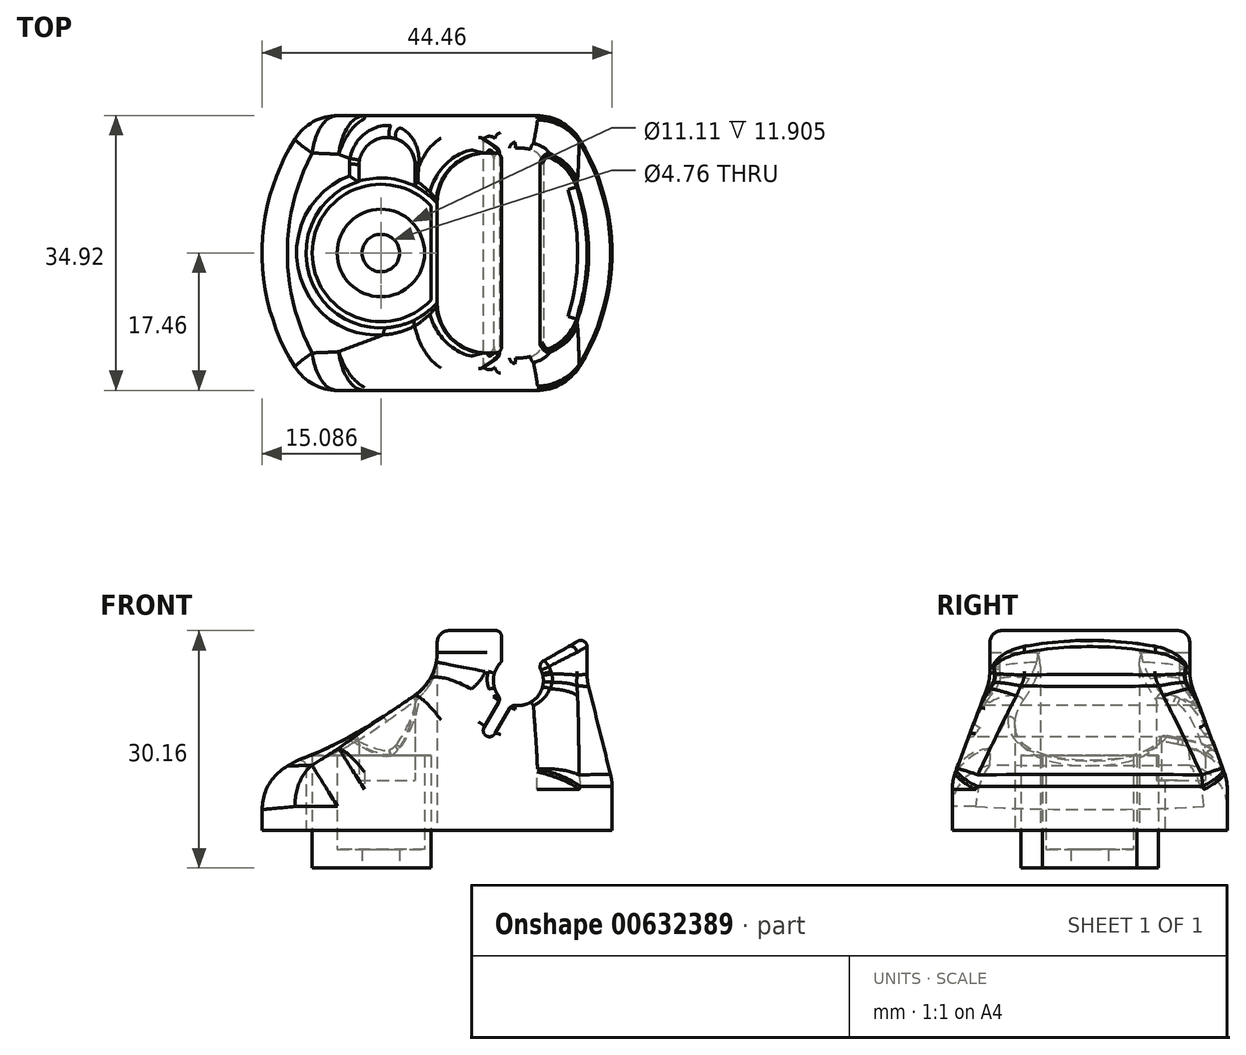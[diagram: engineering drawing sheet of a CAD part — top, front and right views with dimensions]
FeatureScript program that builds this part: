
annotation { "Feature Type Name" : "Feature", "Feature Type Description" : "" }
export const myFeature = defineFeature(function(context is Context, id is Id, definition is map)
    precondition{}
    {
        {
            var Q0;
            Q0=qCreatedBy(makeId("Top.planeOp"),FACE);
            var sketch = newSketch(context, id + "F0", { "sketchPlane" : qUnion([Q0])});
            skLineSegment(sketch, "E0.bottom", {"start": v(22.23, 17.46) * mm, "end": v(15.88, 17.46) * mm, "construction": true});
            skLineSegment(sketch, "E0.top", {"start": v(22.23, -17.46) * mm, "end": v(15.88, -17.46) * mm, "construction": true});
            skLineSegment(sketch, "E0.left", {"start": v(22.23, 17.46) * mm, "end": v(22.23, -17.46) * mm, "construction": true});
            skLineSegment(sketch, "E0.right", {"start": v(-22.22, 17.46) * mm, "end": v(-22.22, -17.46) * mm, "construction": true});
            skPoint(sketch, "E0.middle", {"position": v(0, 0) * mm});
            skArc(sketch, "E1", {"start": v(15.88, -17.46) * mm, "mid": v(22.23, 0) * mm, "end": v(15.88, 17.46) * mm});
            skLineSegment(sketch, "E2", {"start": v(15.88, 17.46) * mm, "end": v(-15.87, 17.46) * mm});
            skLineSegment(sketch, "E3", {"start": v(15.88, -17.46) * mm, "end": v(-15.87, -17.46) * mm});
            skPoint(sketch, "E4.visualSharp", {"position": v(15.88, 17.46) * mm});
            skPoint(sketch, "E5.visualSharp", {"position": v(15.88, -17.46) * mm});
            skArc(sketch, "E6", {"start": v(-15.88, 17.46) * mm, "mid": v(-22.22, 0) * mm, "end": v(-15.87, -17.46) * mm});
            skLineSegment(sketch, "E7", {"start": v(-15.87, 17.46) * mm, "end": v(-22.22, 17.46) * mm, "construction": true});
            skLineSegment(sketch, "E8", {"start": v(-15.87, -17.46) * mm, "end": v(-22.22, -17.46) * mm, "construction": true});
            skPoint(sketch, "E9.visualSharp", {"position": v(-15.87, 17.46) * mm});
            skPoint(sketch, "E10.visualSharp", {"position": v(-15.87, -17.46) * mm});
            skSolve(sketch);
        }
        {
            var Q0;
            Q0=makeQuery(id+"F0.imprint","IMPRINT",FACE,{"disambiguationData":[TD([[makeQuery(id+"F0.imprint","IMPRINT",EDGE,{"derivedFrom":sQuery(id+"F0.wireOp",EDGE,"E1")}),1.0]])]});
            extrude(context, id + "F1", {"entities" : qUnion([Q0]), "depth" : 6.35 * mm, "offsetDistance" : 25.4 * mm});
        }
        {
            var Q0;
            Q0=qCreatedBy(makeId("Top.planeOp"),FACE);
            cPlane(context, id + "F2", {"entities" : qUnion([Q0]), "cplaneType" : CPlaneType.OFFSET, "offset" : 19.05 * mm, "width" : 152.4 * mm, "height" : 152.4 * mm});
        }
        {
            var Q0;
            Q0=qCreatedBy(id+"F2.planeOp",FACE);
            var sketch = newSketch(context, id + "F3", { "sketchPlane" : qUnion([Q0])});
            skLineSegment(sketch, "E11.bottom", {"start": v(0, 12.7) * mm, "end": v(15.9, 12.7) * mm});
            skLineSegment(sketch, "E11.top", {"start": v(0, -12.7) * mm, "end": v(15.9, -12.7) * mm});
            skLineSegment(sketch, "E11.left", {"start": v(0, 12.7) * mm, "end": v(0, -12.7) * mm});
            skLineSegment(sketch, "E11.right", {"start": v(19.05, 12.7) * mm, "end": v(19.05, -12.7) * mm, "construction": true});
            skArc(sketch, "E12", {"start": v(15.9, -12.7) * mm, "mid": v(19.05, 0) * mm, "end": v(15.9, 12.7) * mm});
            skPoint(sketch, "E13.visualSharp", {"position": v(0, 12.7) * mm});
            skPoint(sketch, "E14.visualSharp", {"position": v(0, -12.7) * mm});
            skSolve(sketch);
        }
        {
            var Q1;
            Q1=makeQuery(id+"F1.opExtrude","CAP_FACE",FACE,{"disambiguationData":[OSD([sQuery(id+"F0.wireOp",EDGE,"E1"),sQuery(id+"F0.wireOp",EDGE,"E2"),sQuery(id+"F0.wireOp",EDGE,"E3"),sQuery(id+"F0.wireOp",EDGE,"E4.filletArc"),sQuery(id+"F0.wireOp",EDGE,"E5.filletArc"),sQuery(id+"F0.wireOp",EDGE,"E6"),sQuery(id+"F0.wireOp",EDGE,"E9.filletArc"),sQuery(id+"F0.wireOp",EDGE,"E10.filletArc")])],"isStart":false});
            var Q2;
            Q2=makeQuery(id+"F3.imprint","IMPRINT",FACE,{"disambiguationData":[TD([[makeQuery(id+"F3.imprint","IMPRINT",EDGE,{"derivedFrom":sQuery(id+"F3.wireOp",EDGE,"E11.bottom")}),-1.0]])]});
            loft(context, id + "F4", {"operationType" : NewBodyOperationType.ADD, "sheetProfilesArray" : [{ "sheetProfileEntities" : qUnion([Q1]) }, { "sheetProfileEntities" : qUnion([Q2]) }]});
        }
        {
            var Q0;
            Q0=makeQuery(id+"F4.opLoft","CAP_FACE",FACE,{"disambiguationData":[OSD([makeQuery(id+"F3.imprint","IMPRINT",FACE,{"disambiguationData":[TD([[makeQuery(id+"F3.imprint","IMPRINT",EDGE,{"derivedFrom":sQuery(id+"F3.wireOp",EDGE,"E11.bottom")}),-1.0]])]})])],"isStart":true});
            extrude(context, id + "F5", {"entities" : qUnion([Q0]), "operationType" : NewBodyOperationType.ADD, "flatOperationType" : FlatOperationType.REMOVE, "depth" : 6.35 * mm, "offsetDistance" : 25.4 * mm, "domain" : OperationDomain.MODEL});
        }
        {
            var Q0;
            Q0=makeQuery(id+"F4.opLoft","SWEPT_EDGE",EDGE,{"disambiguationData":[OSD([sQuery(id+"F0.wireOp",EDGE,"E2"),sQuery(id+"F0.wireOp",EDGE,"E6"),sQuery(id+"F3.wireOp",EDGE,"E11.bottom"),sQuery(id+"F3.wireOp",EDGE,"E11.left")])]});
            var Q1;
            Q1=makeQuery(id+"F1.opExtrude","SWEPT_EDGE",EDGE,{"disambiguationData":[OSD([sQuery(id+"F0.wireOp",EDGE,"E2"),sQuery(id+"F0.wireOp",EDGE,"E6")])]});
            var Q2;
            Q2=makeQuery(id+"F5.opExtrude","SWEPT_EDGE",EDGE,{"disambiguationData":[OSD([sQuery(id+"F3.wireOp",EDGE,"E11.bottom"),sQuery(id+"F3.wireOp",EDGE,"E11.left")])]});
            var Q3;
            Q3=makeQuery(id+"F4.opLoft","SWEPT_EDGE",EDGE,{"disambiguationData":[OSD([sQuery(id+"F0.wireOp",EDGE,"E3"),sQuery(id+"F0.wireOp",EDGE,"E6"),sQuery(id+"F3.wireOp",EDGE,"E11.top"),sQuery(id+"F3.wireOp",EDGE,"E11.left")])]});
            var Q4;
            Q4=makeQuery(id+"F5.opExtrude","SWEPT_EDGE",EDGE,{"disambiguationData":[OSD([sQuery(id+"F3.wireOp",EDGE,"E11.top"),sQuery(id+"F3.wireOp",EDGE,"E11.left")])]});
            var Q5;
            Q5=makeQuery(id+"F1.opExtrude","SWEPT_EDGE",EDGE,{"disambiguationData":[OSD([sQuery(id+"F0.wireOp",EDGE,"E3"),sQuery(id+"F0.wireOp",EDGE,"E6")])]});
            var Q6;
            Q6=makeQuery(id+"F1.opExtrude","SWEPT_EDGE",EDGE,{"disambiguationData":[OSD([sQuery(id+"F0.wireOp",EDGE,"E1"),sQuery(id+"F0.wireOp",EDGE,"E3")])]});
            var Q7;
            Q7=makeQuery(id+"F4.opLoft","SWEPT_EDGE",EDGE,{"disambiguationData":[OSD([sQuery(id+"F0.wireOp",EDGE,"E1"),sQuery(id+"F0.wireOp",EDGE,"E3"),sQuery(id+"F3.wireOp",EDGE,"E11.top"),sQuery(id+"F3.wireOp",EDGE,"E12")])]});
            var Q8;
            Q8=makeQuery(id+"F5.opExtrude","SWEPT_EDGE",EDGE,{"disambiguationData":[OSD([sQuery(id+"F3.wireOp",EDGE,"E11.top"),sQuery(id+"F3.wireOp",EDGE,"E12")])]});
            var Q9;
            Q9=makeQuery(id+"F1.opExtrude","SWEPT_EDGE",EDGE,{"disambiguationData":[OSD([sQuery(id+"F0.wireOp",EDGE,"E1"),sQuery(id+"F0.wireOp",EDGE,"E2")])]});
            var Q10;
            Q10=makeQuery(id+"F4.opLoft","SWEPT_EDGE",EDGE,{"disambiguationData":[OSD([sQuery(id+"F0.wireOp",EDGE,"E1"),sQuery(id+"F0.wireOp",EDGE,"E2"),sQuery(id+"F3.wireOp",EDGE,"E11.bottom"),sQuery(id+"F3.wireOp",EDGE,"E12")])]});
            var Q11;
            Q11=makeQuery(id+"F5.opExtrude","SWEPT_EDGE",EDGE,{"disambiguationData":[OSD([sQuery(id+"F3.wireOp",EDGE,"E11.bottom"),sQuery(id+"F3.wireOp",EDGE,"E12")])]});
            var Q12;
            Q12=makeQuery(id+"F4.opLoft","SWEPT_FACE",FACE,{"disambiguationData":[OSD([sQuery(id+"F0.wireOp",EDGE,"E1"),sQuery(id+"F0.wireOp",EDGE,"E2"),sQuery(id+"F0.wireOp",EDGE,"E3"),sQuery(id+"F3.wireOp",EDGE,"E11.bottom"),sQuery(id+"F3.wireOp",EDGE,"E11.top"),sQuery(id+"F3.wireOp",EDGE,"E12")])]});
            var Q13;
            Q13=makeQuery(id+"F4.opLoft","SWEPT_FACE",FACE,{"disambiguationData":[OSD([sQuery(id+"F0.wireOp",EDGE,"E1"),sQuery(id+"F0.wireOp",EDGE,"E2"),sQuery(id+"F0.wireOp",EDGE,"E6"),sQuery(id+"F3.wireOp",EDGE,"E11.bottom"),sQuery(id+"F3.wireOp",EDGE,"E11.left"),sQuery(id+"F3.wireOp",EDGE,"E12")])]});
            var Q14;
            Q14=makeQuery(id+"F4.opLoft","SWEPT_FACE",FACE,{"disambiguationData":[OSD([sQuery(id+"F0.wireOp",EDGE,"E2"),sQuery(id+"F0.wireOp",EDGE,"E3"),sQuery(id+"F0.wireOp",EDGE,"E6"),sQuery(id+"F3.wireOp",EDGE,"E11.bottom"),sQuery(id+"F3.wireOp",EDGE,"E11.top"),sQuery(id+"F3.wireOp",EDGE,"E11.left")])]});
            var Q15;
            Q15=makeQuery(id+"F4.opLoft","SWEPT_FACE",FACE,{"disambiguationData":[OSD([sQuery(id+"F0.wireOp",EDGE,"E1"),sQuery(id+"F0.wireOp",EDGE,"E3"),sQuery(id+"F0.wireOp",EDGE,"E6"),sQuery(id+"F3.wireOp",EDGE,"E11.top"),sQuery(id+"F3.wireOp",EDGE,"E11.left"),sQuery(id+"F3.wireOp",EDGE,"E12")])]});
            fillet(context, id + "F6", {"entities" : qUnion([Q0, Q1, Q2, Q3, Q4, Q5, Q6, Q7, Q8, Q9, Q10, Q11, Q12, Q13, Q14, Q15]), "radius" : 6.35 * mm, "tangentPropagation" : true, "allowEdgeOverflow" : false});
        }
        {
            var Q0;
            Q0=makeQuery(id+"F5.opExtrude","CAP_EDGE",EDGE,{"disambiguationData":[OSD([sQuery(id+"F3.wireOp",EDGE,"E11.bottom"),sQuery(id+"F3.wireOp",EDGE,"E11.top"),sQuery(id+"F3.wireOp",EDGE,"E11.left")])],"isStart":false});
            fillet(context, id + "F7", {"entities" : qUnion([Q0]), "radius" : 1.59 * mm, "tangentPropagation" : true, "allowEdgeOverflow" : false});
        }
        {
            var Q0;
            Q0=qCreatedBy(makeId("Front.planeOp"),FACE);
            var sketch = newSketch(context, id + "F8", { "sketchPlane" : qUnion([Q0])});
            skArc(sketch, "E15", {"start": v(8.21, 21.42) * mm, "mid": v(7.15, 19.13) * mm, "end": v(8.1, 16.78) * mm});
            skLineSegment(sketch, "E16", {"start": v(22.23, 5.57) * mm, "end": v(22.23, 0) * mm, "construction": true});
            skLineSegment(sketch, "E17", {"start": v(8.21, 21.42) * mm, "end": v(8.21, 25.4) * mm});
            skLineSegment(sketch, "E18", {"start": v(8.1, 16.78) * mm, "end": v(5.97, 13.1) * mm});
            skArc(sketch, "E19", {"start": v(5.97, 13.1) * mm, "mid": v(6.26, 12.01) * mm, "end": v(7.34, 12.3) * mm});
            skLineSegment(sketch, "E20", {"start": v(7.34, 12.3) * mm, "end": v(9.47, 16) * mm});
            skLineSegment(sketch, "E21", {"start": v(6.65, 12.7) * mm, "end": v(10.32, 19.05) * mm, "construction": true});
            skArc(sketch, "E22.trimOffspring", {"start": v(9.47, 16) * mm, "mid": v(13, 17.33) * mm, "end": v(12.75, 21.1) * mm});
            skArc(sketch, "E23", {"start": v(19.05, 23.81) * mm, "mid": v(18.59, 24.94) * mm, "end": v(17.46, 25.4) * mm, "construction": true});
            skFitSpline(sketch, "E24.0", {"points": [v(16.24, 25.4) * mm, v(16.65, 25.4) * mm, v(17.06, 25.4) * mm, v(17.46, 25.4) * mm]});
            skLineSegment(sketch, "E25.0", {"start": v(11.7, 25.4) * mm, "end": v(16.24, 25.4) * mm});
            skLineSegment(sketch, "E26.0", {"start": v(8.21, 25.4) * mm, "end": v(11.7, 25.4) * mm});
            skPoint(sketch, "E27.orphan", {"position": v(6.35, 25.4) * mm});
            skLineSegment(sketch, "E28", {"start": v(12.75, 21.1) * mm, "end": v(20.21, 25.4) * mm});
            skLineSegment(sketch, "E29", {"start": v(20.21, 25.4) * mm, "end": v(17.46, 25.4) * mm});
            skSolve(sketch);
        }
        {
            var Q0;
            Q0=makeQuery(id+"F8.imprint","IMPRINT",FACE,{"disambiguationData":[TD([[makeQuery(id+"F8.imprint","IMPRINT",EDGE,{"derivedFrom":sQuery(id+"F8.wireOp",EDGE,"E15")}),1.0]])]});
            extrude(context, id + "F9", {"entities" : qUnion([Q0]), "operationType" : NewBodyOperationType.REMOVE, "endBound" : BoundingType.SYMMETRIC, "oppositeDirection" : true, "depth" : 50.8 * mm, "offsetDistance" : 25.4 * mm});
        }
        {
            var Q0;
            Q0=makeQuery(id+"F9.boolean.opBoolean","INTERSECT",EDGE,{"derivedFrom":[makeQuery(id+"F7.opFillet","BLEND_FACE",FACE,{"disambiguationData":[OSD([sQuery(id+"F3.wireOp",EDGE,"E11.bottom"),sQuery(id+"F3.wireOp",EDGE,"E11.top"),sQuery(id+"F3.wireOp",EDGE,"E12")])]}),makeQuery(id+"F9.opExtrude","SWEPT_FACE",FACE,{"disambiguationData":[OSD([sQuery(id+"F8.wireOp",EDGE,"E28")])]})]});
            var Q1;
            Q1=makeQuery(id+"F9.boolean.opBoolean","COPY",EDGE,{"derivedFrom":makeQuery(id+"F9.opExtrude","SWEPT_EDGE",EDGE,{"disambiguationData":[OSD([sQuery(id+"F8.wireOp",EDGE,"E22.trimOffspring"),sQuery(id+"F8.wireOp",EDGE,"E28")])]})});
            var Q2;
            Q2=makeQuery(id+"F9.boolean.opBoolean","INTERSECT",EDGE,{"derivedFrom":[makeQuery(id+"F6.opFillet","BLEND_FACE",FACE,{"disambiguationData":[OSD([sQuery(id+"F0.wireOp",EDGE,"E1"),sQuery(id+"F0.wireOp",EDGE,"E3")]),OD(1.0)]}),makeQuery(id+"F9.opExtrude","SWEPT_FACE",FACE,{"disambiguationData":[OSD([sQuery(id+"F8.wireOp",EDGE,"E22.trimOffspring")])]})]});
            var Q3;
            Q3=makeQuery(id+"F9.boolean.opBoolean","INTERSECT",EDGE,{"derivedFrom":[makeQuery(id+"F6.opFillet","BLEND_FACE",FACE,{"disambiguationData":[OSD([sQuery(id+"F0.wireOp",EDGE,"E1"),sQuery(id+"F0.wireOp",EDGE,"E2"),sQuery(id+"F3.wireOp",EDGE,"E11.bottom"),sQuery(id+"F3.wireOp",EDGE,"E12")])]}),makeQuery(id+"F9.opExtrude","SWEPT_FACE",FACE,{"disambiguationData":[OSD([sQuery(id+"F8.wireOp",EDGE,"E22.trimOffspring")])]})]});
            var Q4;
            Q4=makeQuery(id+"F9.boolean.opBoolean","COPY",FACE,{"derivedFrom":makeQuery(id+"F9.opExtrude","SWEPT_FACE",FACE,{"disambiguationData":[OSD([sQuery(id+"F8.wireOp",EDGE,"E20")])]})});
            var Q5;
            Q5=makeQuery(id+"F9.boolean.opBoolean","COPY",FACE,{"derivedFrom":makeQuery(id+"F9.opExtrude","SWEPT_FACE",FACE,{"disambiguationData":[OSD([sQuery(id+"F8.wireOp",EDGE,"E15")])]})});
            var Q6;
            Q6=makeQuery(id+"F9.boolean.opBoolean","COPY",EDGE,{"derivedFrom":makeQuery(id+"F9.opExtrude","SWEPT_EDGE",EDGE,{"disambiguationData":[OSD([sQuery(id+"F8.wireOp",EDGE,"E15"),sQuery(id+"F8.wireOp",EDGE,"E17")])]})});
            var Q7;
            Q7=makeQuery(id+"F9.boolean.opBoolean","COPY",FACE,{"derivedFrom":makeQuery(id+"F9.opExtrude","SWEPT_FACE",FACE,{"disambiguationData":[OSD([sQuery(id+"F8.wireOp",EDGE,"E17")])]})});
            fillet(context, id + "F10", {"entities" : qUnion([Q0, Q1, Q2, Q3, Q4, Q5, Q6, Q7]), "radius" : 0.8 * mm, "tangentPropagation" : true, "allowEdgeOverflow" : false});
        }
        {
            var Q0;
            Q0=makeQuery(id+"F1.opExtrude","CAP_FACE",FACE,{"disambiguationData":[OSD([sQuery(id+"F0.wireOp",EDGE,"E1"),sQuery(id+"F0.wireOp",EDGE,"E2"),sQuery(id+"F0.wireOp",EDGE,"E3"),sQuery(id+"F0.wireOp",EDGE,"E6")])],"isStart":true});
            var sketch = newSketch(context, id + "F11", { "sketchPlane" : qUnion([Q0])});
            skPoint(sketch, "E30.middle", {"position": v(-7.14, 0) * mm});
            skCircle(sketch, "E31", {"center": v(-7.14, 0) * mm, "radius": 5.56 * mm, "construction": true});
            skArc(sketch, "E32", {"start": v(0, 6.3) * mm, "mid": v(-16.67, 0) * mm, "end": v(0, -6.3) * mm});
            skLineSegment(sketch, "E33", {"start": v(0, 6.3) * mm, "end": v(0, -6.3) * mm});
            skSolve(sketch);
        }
        {
            var Q0;
            Q0=makeQuery(id+"F11.imprint","IMPRINT",FACE,{"disambiguationData":[TD([[makeQuery(id+"F11.imprint","IMPRINT",EDGE,{"derivedFrom":sQuery(id+"F11.wireOp",EDGE,"E32")}),1.0]])]});
            extrude(context, id + "F12", {"entities" : qUnion([Q0]), "operationType" : NewBodyOperationType.REMOVE, "oppositeDirection" : true, "depth" : 25.4 * mm, "offsetDistance" : 25.4 * mm});
        }
        {
            var Q0;
            Q0=makeQuery(id+"F1.opExtrude","CAP_FACE",FACE,{"disambiguationData":[OSD([sQuery(id+"F0.wireOp",EDGE,"E1"),sQuery(id+"F0.wireOp",EDGE,"E2"),sQuery(id+"F0.wireOp",EDGE,"E3"),sQuery(id+"F0.wireOp",EDGE,"E6")])],"isStart":true});
            cPlane(context, id + "F13", {"entities" : qUnion([Q0]), "cplaneType" : CPlaneType.OFFSET, "offset" : 6.35 * mm, "oppositeDirection" : true, "width" : 152.4 * mm, "height" : 152.4 * mm});
        }
        {
            var Q0;
            Q0=qCreatedBy(id+"F13.planeOp",FACE);
            var sketch = newSketch(context, id + "F14", { "sketchPlane" : qUnion([Q0])});
            skLineSegment(sketch, "E34", {"start": v(-6.35, 0) * mm, "end": v(-6.35, -11.11) * mm, "construction": true});
            skArc(sketch, "E35", {"start": v(-9.92, -11.11) * mm, "mid": v(-6.35, -14.68) * mm, "end": v(-2.78, -11.11) * mm});
            skLineSegment(sketch, "E36", {"start": v(-9.92, -11.11) * mm, "end": v(-9.92, 0) * mm});
            skLineSegment(sketch, "E37", {"start": v(-9.92, 0) * mm, "end": v(-2.78, 0) * mm});
            skLineSegment(sketch, "E38", {"start": v(-2.78, 0) * mm, "end": v(-2.78, -11.11) * mm});
            skSolve(sketch);
        }
        {
            var Q0;
            Q0=makeQuery(id+"F14.imprint","IMPRINT",FACE,{"disambiguationData":[TD([[makeQuery(id+"F14.imprint","IMPRINT",EDGE,{"derivedFrom":sQuery(id+"F14.wireOp",EDGE,"E35")}),1.0]])]});
            extrude(context, id + "F15", {"entities" : qUnion([Q0]), "operationType" : NewBodyOperationType.REMOVE, "oppositeDirection" : true, "depth" : 25.4 * mm, "offsetDistance" : 25.4 * mm});
        }
        {
            var Q0;
            Q0=makeQuery(id+"F12.boolean.opBoolean","INTERSECT",EDGE,{"derivedFrom":[makeQuery(id+"F4.opLoft","SWEPT_FACE",FACE,{"disambiguationData":[OSD([sQuery(id+"F0.wireOp",EDGE,"E2"),sQuery(id+"F0.wireOp",EDGE,"E3"),sQuery(id+"F0.wireOp",EDGE,"E6"),sQuery(id+"F3.wireOp",EDGE,"E11.bottom"),sQuery(id+"F3.wireOp",EDGE,"E11.top"),sQuery(id+"F3.wireOp",EDGE,"E11.left")])]}),makeQuery(id+"F12.opExtrude","SWEPT_FACE",FACE,{"disambiguationData":[OSD([sQuery(id+"F11.wireOp",EDGE,"E32")])]})]});
            var Q1;
            Q1=makeQuery(id+"F15.boolean.opBoolean","INTERSECT",EDGE,{"derivedFrom":[makeQuery(id+"F4.opLoft","SWEPT_FACE",FACE,{"disambiguationData":[OSD([sQuery(id+"F0.wireOp",EDGE,"E2"),sQuery(id+"F0.wireOp",EDGE,"E3"),sQuery(id+"F0.wireOp",EDGE,"E6"),sQuery(id+"F3.wireOp",EDGE,"E11.bottom"),sQuery(id+"F3.wireOp",EDGE,"E11.top"),sQuery(id+"F3.wireOp",EDGE,"E11.left")])]}),makeQuery(id+"F15.opExtrude","SWEPT_FACE",FACE,{"disambiguationData":[OSD([sQuery(id+"F14.wireOp",EDGE,"E36")])]})]});
            var Q2;
            Q2=makeQuery(id+"F12.boolean.opBoolean","INTERSECT",EDGE,{"disambiguationData":[OD(2.0)],"derivedFrom":[makeQuery(id+"F6.opFillet","BLEND_FACE",FACE,{"disambiguationData":[OSD([sQuery(id+"F3.wireOp",EDGE,"E11.bottom"),sQuery(id+"F3.wireOp",EDGE,"E11.top"),sQuery(id+"F3.wireOp",EDGE,"E11.left")])]}),makeQuery(id+"F12.opExtrude","SWEPT_FACE",FACE,{"disambiguationData":[OSD([sQuery(id+"F11.wireOp",EDGE,"E32")])]})]});
            var Q3;
            Q3=makeQuery(id+"Fa9YRneLped70sL_1.1.F15.boolean.opBoolean","INTERSECT",EDGE,{"derivedFrom":[makeQuery(id+"F4.opLoft","SWEPT_FACE",FACE,{"disambiguationData":[OSD([sQuery(id+"F0.wireOp",EDGE,"E2"),sQuery(id+"F0.wireOp",EDGE,"E3"),sQuery(id+"F0.wireOp",EDGE,"E6"),sQuery(id+"F3.wireOp",EDGE,"E11.bottom"),sQuery(id+"F3.wireOp",EDGE,"E11.top"),sQuery(id+"F3.wireOp",EDGE,"E11.left")])]}),makeQuery(id+"Fa9YRneLped70sL_1.1.F15.opExtrude","SWEPT_FACE",FACE,{"disambiguationData":[OSD([sQuery(id+"F14.wireOp",EDGE,"E36")])]})]});
            var Q4;
            Q4=makeQuery(id+"F12.boolean.opBoolean","INTERSECT",EDGE,{"disambiguationData":[OD(3.0)],"derivedFrom":[makeQuery(id+"F6.opFillet","BLEND_FACE",FACE,{"disambiguationData":[OSD([sQuery(id+"F3.wireOp",EDGE,"E11.bottom"),sQuery(id+"F3.wireOp",EDGE,"E11.top"),sQuery(id+"F3.wireOp",EDGE,"E11.left")])]}),makeQuery(id+"F12.opExtrude","SWEPT_FACE",FACE,{"disambiguationData":[OSD([sQuery(id+"F11.wireOp",EDGE,"E32")])]})]});
            fillet(context, id + "F16", {"entities" : qUnion([Q0, Q1, Q2, Q3, Q4]), "radius" : 0.8 * mm, "tangentPropagation" : true, "allowEdgeOverflow" : false});
        }
        {
            var Q0;
            Q0=makeQuery(id+"F11.imprint","IMPRINT",FACE,{"disambiguationData":[TD([[makeQuery(id+"F11.imprint","IMPRINT",EDGE,{"derivedFrom":sQuery(id+"F11.wireOp",EDGE,"E32")}),-1.0]])]});
            var sketch = newSketch(context, id + "F17", { "sketchPlane" : qUnion([Q0])});
            skCircle(sketch, "E39.0", {"center": v(-7.14, 0) * mm, "radius": 5.56 * mm});
            skArc(sketch, "E40.0", {"start": v(0, 6.3) * mm, "mid": v(-16.67, 0) * mm, "end": v(0, -6.3) * mm, "construction": true});
            skLineSegment(sketch, "E41.0", {"start": v(0, 6.3) * mm, "end": v(0, -6.3) * mm, "construction": true});
            skArc(sketch, "E42.0", {"start": v(-0.8, 6) * mm, "mid": v(-15.87, 0) * mm, "end": v(-0.8, -6) * mm});
            skLineSegment(sketch, "E42.1", {"start": v(-0.8, 6) * mm, "end": v(-0.8, -6) * mm});
            skSolve(sketch);
        }
        {
            var Q0;
            Q0=makeQuery(id+"F17.imprint","IMPRINT",FACE,{"disambiguationData":[TD([[makeQuery(id+"F17.imprint","IMPRINT",EDGE,{"derivedFrom":sQuery(id+"F17.wireOp",EDGE,"E39.0")}),-1.0]])]});
            var Q1;
            Q1=makeQuery(id+"F15.boolean.opBoolean","COPY",FACE,{"derivedFrom":makeQuery(id+"F15.opExtrude","CAP_FACE",FACE,{"disambiguationData":[OSD([sQuery(id+"F14.wireOp",EDGE,"E35"),sQuery(id+"F14.wireOp",EDGE,"E36"),sQuery(id+"F14.wireOp",EDGE,"E37"),sQuery(id+"F14.wireOp",EDGE,"E38")])],"isStart":true})});
            extrude(context, id + "F18", {"entities" : qUnion([Q0]), "endBound" : BoundingType.UP_TO_SURFACE, "oppositeDirection" : true, "depth" : 25.4 * mm, "endBoundEntityFace" : qUnion([Q1]), "offsetDistance" : 0 * mm});
        }
        {
            var Q0;
            Q0=makeQuery(id+"F18.opExtrude","CAP_FACE",FACE,{"disambiguationData":[OSD([sQuery(id+"F17.wireOp",EDGE,"E39.0"),sQuery(id+"F17.wireOp",EDGE,"E42.0"),sQuery(id+"F17.wireOp",EDGE,"E42.1")])],"isStart":false});
            var sketch = newSketch(context, id + "F19", { "sketchPlane" : qUnion([Q0])});
            skLineSegment(sketch, "E43.0", {"start": v(-9.53, 11.11) * mm, "end": v(-9.53, 5.02) * mm});
            skArc(sketch, "E43.1", {"start": v(-9.53, 11.11) * mm, "mid": v(-6.35, 14.29) * mm, "end": v(-3.18, 11.11) * mm});
            skLineSegment(sketch, "E43.2", {"start": v(-3.18, 3.89) * mm, "end": v(-3.18, 11.11) * mm});
            skArc(sketch, "E44.0", {"start": v(-3.18, 3.89) * mm, "mid": v(-6.17, 5.47) * mm, "end": v(-9.53, 5.02) * mm});
            skSolve(sketch);
        }
        {
            var Q0;
            {var subQ0=sQuery(id+"F19.wireOp",EDGE,"E43.1");Q0=makeQuery(id+"F19.imprint","IMPRINT",FACE,{"disambiguationData":[TD([[makeQuery(id+"F19.imprint","IMPRINT",EDGE,{"derivedFrom":subQ0}),-1.0]])]});}
            var Q1;
            {var subQ0=sQuery(id+"F19.wireOp",EDGE,"E44.0");Q1=makeQuery(id+"F19.imprint","IMPRINT",FACE,{"disambiguationData":[TD([[makeQuery(id+"F19.imprint","IMPRINT",EDGE,{"derivedFrom":subQ0}),-1.0]])]});}
            extrude(context, id + "F20", {"entities" : qUnion([Q0, Q1]), "operationType" : NewBodyOperationType.ADD, "depth" : 3.17 * mm, "offsetDistance" : 25.4 * mm});
        }
        {
            var Q0;
            {var subQ3=sQuery(id+"F19.wireOp",EDGE,"E43.0");var subQ4=sQuery(id+"F17.wireOp",EDGE,"E42.0");var subQ5=sQuery(id+"F17.wireOp",EDGE,"E39.0");Q0=makeQuery(id+"FMi2Dvn2P8TACtl_2.1.F20.boolean.opBoolean","SPLIT",FACE,{"disambiguationData":[TD([makeQuery(id+"F20.opExtrude","SWEPT_FACE",FACE,{"disambiguationData":[OSD([subQ3])]})])],"derivedFrom":makeQuery(id+"F18.opExtrude","CAP_FACE",FACE,{"disambiguationData":[OSD([subQ5,subQ4,sQuery(id+"F17.wireOp",EDGE,"E42.1")])],"isStart":false})});}
            var Q1;
            {var subQ4=sQuery(id+"F17.wireOp",EDGE,"E42.1");var subQ5=sQuery(id+"F17.wireOp",EDGE,"E42.0");var subQ6=sQuery(id+"F17.wireOp",EDGE,"E39.0");Q1=makeQuery(id+"FMi2Dvn2P8TACtl_2.1.F20.boolean.opBoolean","SPLIT",FACE,{"disambiguationData":[TD([makeQuery(id+"F18.opExtrude","SWEPT_FACE",FACE,{"disambiguationData":[OSD([subQ4])]})])],"derivedFrom":makeQuery(id+"F18.opExtrude","CAP_FACE",FACE,{"disambiguationData":[OSD([subQ6,subQ5,subQ4])],"isStart":false})});}
            var Q2;
            Q2=makeQuery(id+"F20.opExtrude","CAP_FACE",FACE,{"disambiguationData":[OSD([sQuery(id+"F19.wireOp",EDGE,"E43.0"),sQuery(id+"F19.wireOp",EDGE,"E43.1"),sQuery(id+"F19.wireOp",EDGE,"E43.2"),sQuery(id+"F19.wireOp",EDGE,"E44.0")])],"isStart":false});
            extrude(context, id + "F21", {"entities" : qUnion([Q0, Q1]), "operationType" : NewBodyOperationType.ADD, "endBound" : BoundingType.UP_TO_SURFACE, "depth" : 25.4 * mm, "endBoundEntityFace" : qUnion([Q2]), "offsetDistance" : 25.4 * mm});
        }
        {
            var Q0;
            Q0=qCreatedBy(makeId("Top.planeOp"),FACE);
            var sketch = newSketch(context, id + "F22", { "sketchPlane" : qUnion([Q0])});
            skArc(sketch, "E45.0", {"start": v(-0.8, -6) * mm, "mid": v(-15.87, 0) * mm, "end": v(-0.8, 6) * mm});
            skLineSegment(sketch, "E46.0", {"start": v(-0.8, -6) * mm, "end": v(-0.8, 6) * mm});
            skSolve(sketch);
        }
        {
            var Q0;
            Q0 = qSketchRegion(id + "F22", true);
            extrude(context, id + "F23", {"entities" : qUnion([Q0]), "operationType" : NewBodyOperationType.ADD, "oppositeDirection" : true, "depth" : 4.76 * mm, "offsetDistance" : 25.4 * mm});
        }
        {
            var Q0;
            Q0=makeQuery(id+"F23.opExtrude","CAP_FACE",FACE,{"disambiguationData":[OSD([sQuery(id+"F22.wireOp",EDGE,"E45.0"),sQuery(id+"F22.wireOp",EDGE,"E46.0")])],"isStart":false});
            var sketch = newSketch(context, id + "F24", { "sketchPlane" : qUnion([Q0])});
            skCircle(sketch, "E47", {"center": v(-7.14, 0) * mm, "radius": 2.38 * mm});
            skSolve(sketch);
        }
        {
            var Q0;
            Q0=makeQuery(id+"F24.imprint","IMPRINT",FACE,{"disambiguationData":[TD([[makeQuery(id+"F24.imprint","IMPRINT",EDGE,{"derivedFrom":sQuery(id+"F24.wireOp",EDGE,"E47")}),1.0]])]});
            extrude(context, id + "F25", {"entities" : qUnion([Q0]), "operationType" : NewBodyOperationType.REMOVE, "oppositeDirection" : true, "depth" : 25.4 * mm, "offsetDistance" : 25.4 * mm});
        }
        {
            var Q0;
            Q0=makeQuery(id+"F11.imprint","IMPRINT",FACE,{"disambiguationData":[TD([[makeQuery(id+"F11.imprint","IMPRINT",EDGE,{"derivedFrom":sQuery(id+"F11.wireOp",EDGE,"E32")}),-1.0]])]});
            var sketch = newSketch(context, id + "F26", { "sketchPlane" : qUnion([Q0])});
            skCircle(sketch, "E48.0", {"center": v(-7.14, 0) * mm, "radius": 5.56 * mm});
            skSolve(sketch);
        }
        {
            var Q0;
            Q0 = qSketchRegion(id + "F26", true);
            extrude(context, id + "F27", {"entities" : qUnion([Q0]), "operationType" : NewBodyOperationType.REMOVE, "depth" : 2.38 * mm, "offsetDistance" : 25.4 * mm});
        }
    });
